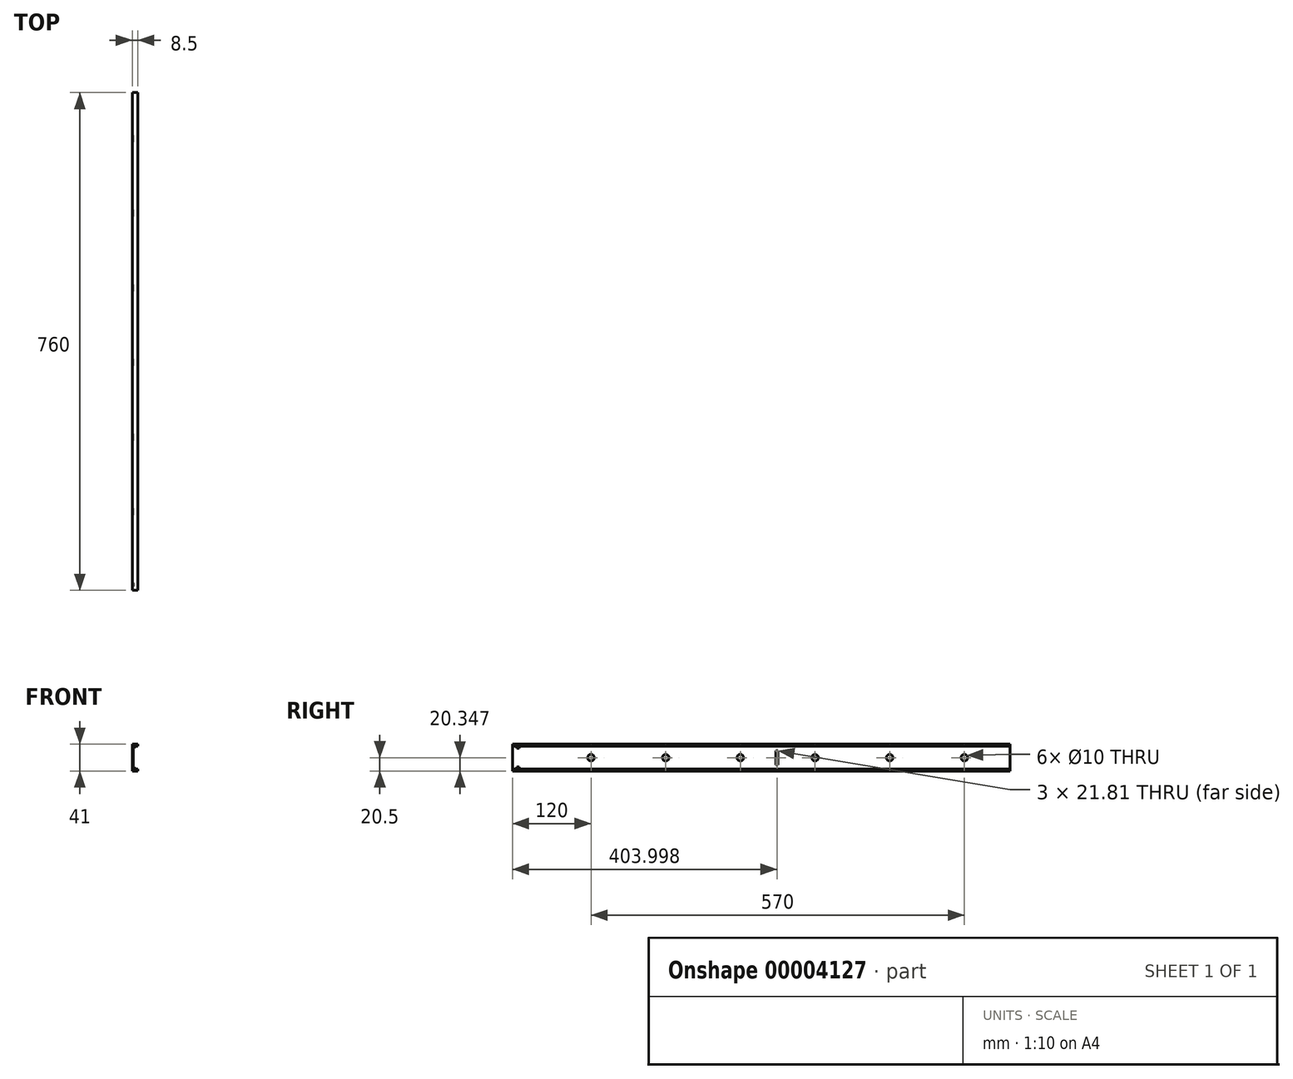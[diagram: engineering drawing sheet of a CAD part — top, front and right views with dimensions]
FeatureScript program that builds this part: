
annotation { "Feature Type Name" : "Feature", "Feature Type Description" : "" }
export const myFeature = defineFeature(function(context is Context, id is Id, definition is map)
    precondition{}
    {
        {
            var Q0;
            Q0=qCreatedBy(makeId("Front.planeOp"),FACE);
            var sketch = newSketch(context, id + "F0", { "sketchPlane" : qUnion([Q0])});
            skLineSegment(sketch, "E0", {"start": v(0, 0) * mm, "end": v(0, 20.5) * mm});
            skLineSegment(sketch, "E1", {"start": v(8.5, 20.5) * mm, "end": v(8.5, 17.5) * mm});
            skLineSegment(sketch, "E2", {"start": v(8.5, 17.5) * mm, "end": v(1.5, 17.5) * mm});
            skLineSegment(sketch, "E3", {"start": v(-18.28, 0) * mm, "end": v(14.41, 0) * mm});
            skLineSegment(sketch, "E4", {"start": v(1.5, 17.5) * mm, "end": v(1.5, 0) * mm});
            skLineSegment(sketch, "E5.0.MirrorCS", {"start": v(1.5, -17.5) * mm, "end": v(1.5, 0) * mm});
            skLineSegment(sketch, "E6.0.MirrorCS", {"start": v(0, 0) * mm, "end": v(0, -20.5) * mm});
            skLineSegment(sketch, "E7.0.MirrorCS", {"start": v(8.5, -17.5) * mm, "end": v(1.5, -17.5) * mm});
            skLineSegment(sketch, "E8.0.MirrorCS", {"start": v(8.5, -20.5) * mm, "end": v(8.5, -17.5) * mm});
            skLineSegment(sketch, "E9.2.MirrorCS", {"start": v(0, -20.5) * mm, "end": v(8.5, -20.5) * mm});
            skLineSegment(sketch, "E10", {"start": v(0, 20.5) * mm, "end": v(8.5, 20.5) * mm});
            skSolve(sketch);
        }
        {
            var Q0;
            {var subQ2=sQuery(id+"F0.wireOp",EDGE,"E0");Q0=makeQuery(id+"F0.imprint","IMPRINT",FACE,{"disambiguationData":[TD([[makeQuery(id+"F0.imprint","IMPRINT",EDGE,{"derivedFrom":subQ2}),-1.0]])]});}
            var Q1;
            {var subQ1=sQuery(id+"F0.wireOp",EDGE,"E5.0.MirrorCS");Q1=makeQuery(id+"F0.imprint","IMPRINT",FACE,{"disambiguationData":[TD([[makeQuery(id+"F0.imprint","IMPRINT",EDGE,{"derivedFrom":subQ1}),1.0]])]});}
            extrude(context, id + "F1", {"entities" : qUnion([Q0, Q1]), "depth" : 760 * mm});
        }
        {
            var Q0;
            Q0=makeQuery(id+"F1.opExtrude","SWEPT_FACE",FACE,{"disambiguationData":[OSD([sQuery(id+"F0.wireOp",EDGE,"E4"),sQuery(id+"F0.wireOp",EDGE,"E5.0.MirrorCS")])]});
            var sketch = newSketch(context, id + "F2", { "sketchPlane" : qUnion([Q0])});
            skLineSegment(sketch, "E11", {"start": v(-760, 0) * mm, "end": v(0, 0) * mm});
            skCircle(sketch, "E12", {"center": v(-70, 0) * mm, "radius": 5 * mm});
            skCircle(sketch, "E13.1.0.0", {"center": v(-184, 0) * mm, "radius": 5 * mm});
            skCircle(sketch, "E13.2.0.0", {"center": v(-298, 0) * mm, "radius": 5 * mm});
            skCircle(sketch, "E13.3.0.0", {"center": v(-412, 0) * mm, "radius": 5 * mm});
            skCircle(sketch, "E13.4.0.0", {"center": v(-526, 0) * mm, "radius": 5 * mm});
            skCircle(sketch, "E13.5.0.0", {"center": v(-640, 0) * mm, "radius": 5 * mm});
            skLineSegment(sketch, "E13.direction1", {"start": v(-70, 0) * mm, "end": v(-184, 0) * mm, "construction": true});
            skSolve(sketch);
        }
        {
            var Q0;
            {var subQ0=sQuery(id+"F2.wireOp",EDGE,"E13.5.0.0");var subQ1=sQuery(id+"F2.wireOp",EDGE,"E11");var subQ3=makeQuery(id+"F2.imprint","INTERSECT",VERTEX,{"disambiguationData":[OD(0.0)],"derivedFrom":[subQ1,subQ0]});Q0=makeQuery(id+"F2.imprint","IMPRINT",FACE,{"disambiguationData":[TD([[makeQuery(id+"F2.imprint","IMPRINT",EDGE,{"disambiguationData":[TD([[subQ3,-1.0]])],"derivedFrom":subQ1}),-1.0]])]});}
            var Q1;
            {var subQ0=sQuery(id+"F2.wireOp",EDGE,"E13.5.0.0");var subQ1=sQuery(id+"F2.wireOp",EDGE,"E11");var subQ3=makeQuery(id+"F2.imprint","INTERSECT",VERTEX,{"disambiguationData":[OD(0.0)],"derivedFrom":[subQ1,subQ0]});Q1=makeQuery(id+"F2.imprint","IMPRINT",FACE,{"disambiguationData":[TD([[makeQuery(id+"F2.imprint","IMPRINT",EDGE,{"disambiguationData":[TD([[subQ3,-1.0]])],"derivedFrom":subQ1}),1.0]])]});}
            var Q2;
            {var subQ0=sQuery(id+"F2.wireOp",EDGE,"E13.4.0.0");var subQ1=sQuery(id+"F2.wireOp",EDGE,"E11");var subQ3=makeQuery(id+"F2.imprint","INTERSECT",VERTEX,{"disambiguationData":[OD(0.0)],"derivedFrom":[subQ1,subQ0]});Q2=makeQuery(id+"F2.imprint","IMPRINT",FACE,{"disambiguationData":[TD([[makeQuery(id+"F2.imprint","IMPRINT",EDGE,{"disambiguationData":[TD([[subQ3,-1.0]])],"derivedFrom":subQ1}),-1.0]])]});}
            var Q3;
            {var subQ0=sQuery(id+"F2.wireOp",EDGE,"E13.4.0.0");var subQ1=sQuery(id+"F2.wireOp",EDGE,"E11");var subQ3=makeQuery(id+"F2.imprint","INTERSECT",VERTEX,{"disambiguationData":[OD(0.0)],"derivedFrom":[subQ1,subQ0]});Q3=makeQuery(id+"F2.imprint","IMPRINT",FACE,{"disambiguationData":[TD([[makeQuery(id+"F2.imprint","IMPRINT",EDGE,{"disambiguationData":[TD([[subQ3,-1.0]])],"derivedFrom":subQ1}),1.0]])]});}
            var Q4;
            {var subQ0=sQuery(id+"F2.wireOp",EDGE,"E13.3.0.0");var subQ1=sQuery(id+"F2.wireOp",EDGE,"E11");var subQ3=makeQuery(id+"F2.imprint","INTERSECT",VERTEX,{"disambiguationData":[OD(0.0)],"derivedFrom":[subQ1,subQ0]});Q4=makeQuery(id+"F2.imprint","IMPRINT",FACE,{"disambiguationData":[TD([[makeQuery(id+"F2.imprint","IMPRINT",EDGE,{"disambiguationData":[TD([[subQ3,-1.0]])],"derivedFrom":subQ1}),-1.0]])]});}
            var Q5;
            {var subQ0=sQuery(id+"F2.wireOp",EDGE,"E13.3.0.0");var subQ1=sQuery(id+"F2.wireOp",EDGE,"E11");var subQ3=makeQuery(id+"F2.imprint","INTERSECT",VERTEX,{"disambiguationData":[OD(0.0)],"derivedFrom":[subQ1,subQ0]});Q5=makeQuery(id+"F2.imprint","IMPRINT",FACE,{"disambiguationData":[TD([[makeQuery(id+"F2.imprint","IMPRINT",EDGE,{"disambiguationData":[TD([[subQ3,-1.0]])],"derivedFrom":subQ1}),1.0]])]});}
            var Q6;
            {var subQ0=sQuery(id+"F2.wireOp",EDGE,"E13.2.0.0");var subQ1=sQuery(id+"F2.wireOp",EDGE,"E11");var subQ3=makeQuery(id+"F2.imprint","INTERSECT",VERTEX,{"disambiguationData":[OD(0.0)],"derivedFrom":[subQ1,subQ0]});Q6=makeQuery(id+"F2.imprint","IMPRINT",FACE,{"disambiguationData":[TD([[makeQuery(id+"F2.imprint","IMPRINT",EDGE,{"disambiguationData":[TD([[subQ3,-1.0]])],"derivedFrom":subQ1}),-1.0]])]});}
            var Q7;
            {var subQ0=sQuery(id+"F2.wireOp",EDGE,"E13.2.0.0");var subQ1=sQuery(id+"F2.wireOp",EDGE,"E11");var subQ3=makeQuery(id+"F2.imprint","INTERSECT",VERTEX,{"disambiguationData":[OD(0.0)],"derivedFrom":[subQ1,subQ0]});Q7=makeQuery(id+"F2.imprint","IMPRINT",FACE,{"disambiguationData":[TD([[makeQuery(id+"F2.imprint","IMPRINT",EDGE,{"disambiguationData":[TD([[subQ3,-1.0]])],"derivedFrom":subQ1}),1.0]])]});}
            var Q8;
            {var subQ0=sQuery(id+"F2.wireOp",EDGE,"E13.1.0.0");var subQ1=sQuery(id+"F2.wireOp",EDGE,"E11");var subQ3=makeQuery(id+"F2.imprint","INTERSECT",VERTEX,{"disambiguationData":[OD(0.0)],"derivedFrom":[subQ1,subQ0]});Q8=makeQuery(id+"F2.imprint","IMPRINT",FACE,{"disambiguationData":[TD([[makeQuery(id+"F2.imprint","IMPRINT",EDGE,{"disambiguationData":[TD([[subQ3,-1.0]])],"derivedFrom":subQ1}),-1.0]])]});}
            var Q9;
            {var subQ0=sQuery(id+"F2.wireOp",EDGE,"E13.1.0.0");var subQ1=sQuery(id+"F2.wireOp",EDGE,"E11");var subQ3=makeQuery(id+"F2.imprint","INTERSECT",VERTEX,{"disambiguationData":[OD(0.0)],"derivedFrom":[subQ1,subQ0]});Q9=makeQuery(id+"F2.imprint","IMPRINT",FACE,{"disambiguationData":[TD([[makeQuery(id+"F2.imprint","IMPRINT",EDGE,{"disambiguationData":[TD([[subQ3,-1.0]])],"derivedFrom":subQ1}),1.0]])]});}
            var Q10;
            {var subQ0=sQuery(id+"F2.wireOp",EDGE,"E12");var subQ1=sQuery(id+"F2.wireOp",EDGE,"E11");var subQ3=makeQuery(id+"F2.imprint","INTERSECT",VERTEX,{"disambiguationData":[OD(0.0)],"derivedFrom":[subQ1,subQ0]});Q10=makeQuery(id+"F2.imprint","IMPRINT",FACE,{"disambiguationData":[TD([[makeQuery(id+"F2.imprint","IMPRINT",EDGE,{"disambiguationData":[TD([[subQ3,-1.0]])],"derivedFrom":subQ1}),1.0]])]});}
            var Q11;
            {var subQ0=sQuery(id+"F2.wireOp",EDGE,"E12");var subQ1=sQuery(id+"F2.wireOp",EDGE,"E11");var subQ3=makeQuery(id+"F2.imprint","INTERSECT",VERTEX,{"disambiguationData":[OD(0.0)],"derivedFrom":[subQ1,subQ0]});Q11=makeQuery(id+"F2.imprint","IMPRINT",FACE,{"disambiguationData":[TD([[makeQuery(id+"F2.imprint","IMPRINT",EDGE,{"disambiguationData":[TD([[subQ3,-1.0]])],"derivedFrom":subQ1}),-1.0]])]});}
            extrude(context, id + "F3", {"entities" : qUnion([Q0, Q1, Q2, Q3, Q4, Q5, Q6, Q7, Q8, Q9, Q10, Q11]), "operationType" : NewBodyOperationType.REMOVE, "oppositeDirection" : true, "depth" : 25 * mm});
        }
        {
            var Q0;
            Q0=makeQuery(id+"F1.opExtrude","SWEPT_FACE",FACE,{"disambiguationData":[OSD([sQuery(id+"F0.wireOp",EDGE,"E4"),sQuery(id+"F0.wireOp",EDGE,"E5.0.MirrorCS")])]});
            var sketch = newSketch(context, id + "F4", { "sketchPlane" : qUnion([Q0])});
            skLineSegment(sketch, "E14", {"start": v(-749.5, 17.5) * mm, "end": v(-749.5, -17.5) * mm});
            skLineSegment(sketch, "E15", {"start": v(-749.5, -16) * mm, "end": v(-753.5, -16) * mm});
            skLineSegment(sketch, "E16", {"start": v(-753.5, -16) * mm, "end": v(-753.5, -14.5) * mm});
            skLineSegment(sketch, "E17", {"start": v(-753.5, -14.5) * mm, "end": v(-749.5, -14.5) * mm});
            skLineSegment(sketch, "E18", {"start": v(-760, 0) * mm, "end": v(-742.49, 0) * mm});
            skLineSegment(sketch, "E19.0.MirrorCS", {"start": v(-753.5, 16) * mm, "end": v(-753.5, 14.5) * mm});
            skLineSegment(sketch, "E20.0.MirrorCS", {"start": v(-753.5, 14.5) * mm, "end": v(-749.5, 14.5) * mm});
            skLineSegment(sketch, "E21.0.MirrorCS", {"start": v(-749.5, 16) * mm, "end": v(-753.5, 16) * mm});
            skSolve(sketch);
        }
        {
            var Q0;
            Q0=makeQuery(id+"F4.imprint","IMPRINT",FACE,{"disambiguationData":[TD([[makeQuery(id+"F4.imprint","IMPRINT",EDGE,{"derivedFrom":sQuery(id+"F4.wireOp",EDGE,"E19.0.MirrorCS")}),1.0]])]});
            var Q1;
            {var subQ1=sQuery(id+"F4.wireOp",EDGE,"E15");Q1=makeQuery(id+"F4.imprint","IMPRINT",FACE,{"disambiguationData":[TD([[makeQuery(id+"F4.imprint","IMPRINT",EDGE,{"derivedFrom":subQ1}),-1.0]])]});}
            extrude(context, id + "F5", {"entities" : qUnion([Q0, Q1]), "operationType" : NewBodyOperationType.ADD, "depth" : 2 * mm});
        }
        {
            var Q0;
            Q0=makeQuery(id+"F1.opExtrude","SWEPT_FACE",FACE,{"disambiguationData":[OSD([sQuery(id+"F0.wireOp",EDGE,"E4"),sQuery(id+"F0.wireOp",EDGE,"E5.0.MirrorCS")])]});
            var sketch = newSketch(context, id + "F6", { "sketchPlane" : qUnion([Q0])});
            skLineSegment(sketch, "E22", {"start": v(-749.5, 0) * mm, "end": v(-357.5, 0) * mm});
            skLineSegment(sketch, "E23.bottom", {"start": v(-357.5, 10.75) * mm, "end": v(-354.5, 10.75) * mm});
            skLineSegment(sketch, "E23.top", {"start": v(-357.5, -11.06) * mm, "end": v(-354.5, -11.06) * mm});
            skLineSegment(sketch, "E23.left", {"start": v(-357.5, 10.75) * mm, "end": v(-357.5, -11.06) * mm});
            skLineSegment(sketch, "E23.right", {"start": v(-354.5, 10.75) * mm, "end": v(-354.5, -11.06) * mm});
            skSolve(sketch);
        }
        {
            var Q0;
            {var subQ3=sQuery(id+"F6.wireOp",EDGE,"E23.bottom");Q0=makeQuery(id+"F6.imprint","IMPRINT",FACE,{"disambiguationData":[TD([[makeQuery(id+"F6.imprint","IMPRINT",EDGE,{"derivedFrom":subQ3}),-1.0]])]});}
            extrude(context, id + "F7", {"entities" : qUnion([Q0]), "operationType" : NewBodyOperationType.REMOVE, "oppositeDirection" : true, "depth" : 25 * mm});
        }
    });
